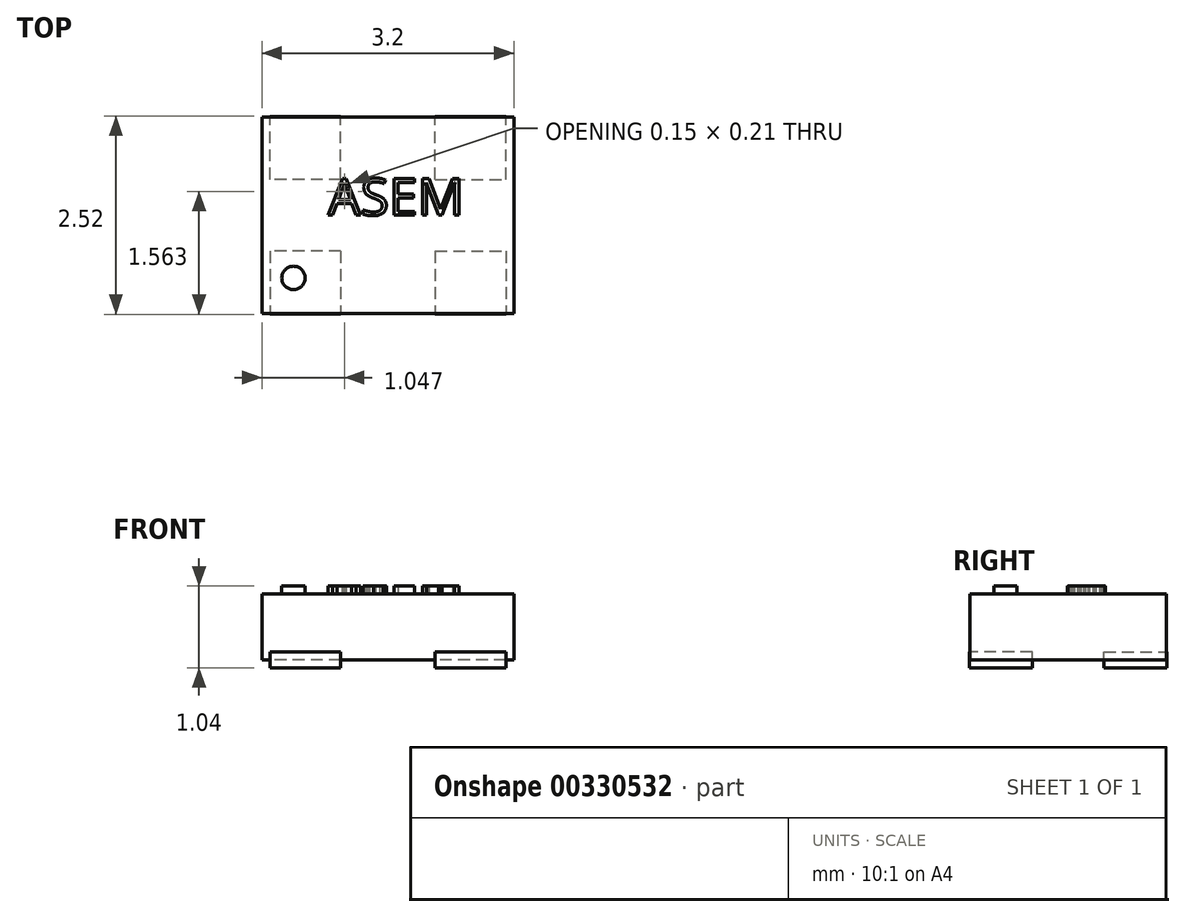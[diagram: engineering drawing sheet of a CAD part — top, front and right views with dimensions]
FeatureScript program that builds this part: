
annotation { "Feature Type Name" : "Feature", "Feature Type Description" : "" }
export const myFeature = defineFeature(function(context is Context, id is Id, definition is map)
    precondition{}
    {
        {
            var Q0;
            Q0=qCreatedBy(makeId("Top.planeOp"),FACE);
            var sketch = newSketch(context, id + "F0", { "sketchPlane" : qUnion([Q0])});
            skLineSegment(sketch, "E0.bottom", {"start": v(1.6, -1.25) * mm, "end": v(-1.6, -1.25) * mm});
            skLineSegment(sketch, "E0.top", {"start": v(1.6, 1.25) * mm, "end": v(-1.6, 1.25) * mm});
            skLineSegment(sketch, "E0.left", {"start": v(1.6, -1.25) * mm, "end": v(1.6, 1.25) * mm});
            skLineSegment(sketch, "E0.right", {"start": v(-1.6, -1.25) * mm, "end": v(-1.6, 1.25) * mm});
            skPoint(sketch, "E0.middle", {"position": v(0, 0) * mm});
            skSolve(sketch);
        }
        {
            var Q0;
            Q0 = qSketchRegion(id + "F0", true);
            extrude(context, id + "F1", {"entities" : qUnion([Q0]), "depth" : .84 * mm, "offsetDistance" : 25 * mm});
        }
        {
            var Q0;
            Q0=makeQuery(id+"F1.opExtrude","CAP_FACE",FACE,{"disambiguationData":[OSD([sQuery(id+"F0.wireOp",EDGE,"E0.bottom"),sQuery(id+"F0.wireOp",EDGE,"E0.top"),sQuery(id+"F0.wireOp",EDGE,"E0.left"),sQuery(id+"F0.wireOp",EDGE,"E0.right")])],"isStart":false});
            var sketch = newSketch(context, id + "F2", { "sketchPlane" : qUnion([Q0])});
            skCircle(sketch, "E1", {"center": v(-1.2, -0.8) * mm, "radius": 0.15 * mm});
            skText(sketch, "E2", { "text": "ASEM", "fontName": "OpenSans-Regular.ttf"});
            const initialGuessF2  = {"E2": [-0.00076, 0, 1, 0, 0.00047]};
            skSetInitialGuess(sketch, initialGuessF2);
            skSolve(sketch);
        }
        {
            var Q0;
            Q0 = qSketchRegion(id + "F2", true);
            extrude(context, id + "F3", {"entities" : qUnion([Q0]), "depth" : .1 * mm, "offsetDistance" : 25 * mm});
        }
        {
            var Q0;
            Q0=makeQuery(id+"F1.opExtrude","CAP_FACE",FACE,{"disambiguationData":[OSD([sQuery(id+"F0.wireOp",EDGE,"E0.bottom"),sQuery(id+"F0.wireOp",EDGE,"E0.top"),sQuery(id+"F0.wireOp",EDGE,"E0.left"),sQuery(id+"F0.wireOp",EDGE,"E0.right")])],"isStart":true});
            var sketch = newSketch(context, id + "F4", { "sketchPlane" : qUnion([Q0])});
            skLineSegment(sketch, "E3.bottom", {"start": v(-0.6, 0.46) * mm, "end": v(-1.5, 0.46) * mm});
            skLineSegment(sketch, "E3.top", {"start": v(-0.6, 1.26) * mm, "end": v(-1.5, 1.26) * mm});
            skLineSegment(sketch, "E3.left", {"start": v(-0.6, 0.46) * mm, "end": v(-0.6, 1.26) * mm});
            skLineSegment(sketch, "E3.right", {"start": v(-1.5, 0.46) * mm, "end": v(-1.5, 1.26) * mm});
            skPoint(sketch, "E3.middle", {"position": v(-1.05, 0.86) * mm});
            skLineSegment(sketch, "E4", {"start": v(0, 0) * mm, "end": v(0, 1.25) * mm, "construction": true});
            skPoint(sketch, "E5.MirrorP", {"position": v(1.05, 0.86) * mm});
            skLineSegment(sketch, "E6.MirrorCS", {"start": v(0.6, 0.46) * mm, "end": v(1.5, 0.46) * mm});
            skLineSegment(sketch, "E7.MirrorCS", {"start": v(0.6, 1.26) * mm, "end": v(1.5, 1.26) * mm});
            skLineSegment(sketch, "E8.MirrorCS", {"start": v(0.6, 0.46) * mm, "end": v(0.6, 1.26) * mm});
            skLineSegment(sketch, "E9.MirrorCS", {"start": v(1.5, 0.46) * mm, "end": v(1.5, 1.26) * mm});
            skLineSegment(sketch, "E10", {"start": v(-1.6, 0) * mm, "end": v(1.68, 0) * mm, "construction": true});
            skPoint(sketch, "E11.MirrorP", {"position": v(1.05, -0.86) * mm});
            skPoint(sketch, "E12.MirrorP", {"position": v(-1.05, -0.86) * mm});
            skLineSegment(sketch, "E13.MirrorCS", {"start": v(-0.6, -0.45) * mm, "end": v(-1.5, -0.46) * mm});
            skLineSegment(sketch, "E14.MirrorCS", {"start": v(-0.6, -1.25) * mm, "end": v(-1.5, -1.25) * mm});
            skLineSegment(sketch, "E15.MirrorCS", {"start": v(-0.6, -0.46) * mm, "end": v(-0.6, -1.25) * mm});
            skLineSegment(sketch, "E16.MirrorCS", {"start": v(0, 0) * mm, "end": v(0, -1.25) * mm, "construction": true});
            skLineSegment(sketch, "E17.MirrorCS", {"start": v(0.6, -0.46) * mm, "end": v(1.5, -0.46) * mm});
            skLineSegment(sketch, "E18.MirrorCS", {"start": v(0.6, -1.26) * mm, "end": v(1.5, -1.26) * mm});
            skLineSegment(sketch, "E19.MirrorCS", {"start": v(0.6, -0.46) * mm, "end": v(0.6, -1.25) * mm});
            skLineSegment(sketch, "E20.MirrorCS", {"start": v(1.5, -0.46) * mm, "end": v(1.5, -1.26) * mm});
            skLineSegment(sketch, "E21.MirrorCS", {"start": v(-1.5, -0.46) * mm, "end": v(-1.5, -1.26) * mm});
            skSolve(sketch);
        }
        {
            var Q0;
            Q0 = qSketchRegion(id + "F4", true);
            extrude(context, id + "F5", {"entities" : qUnion([Q0]), "depth" : .1 * mm, "offsetDistance" : 25 * mm, "hasSecondDirection" : true, "secondDirectionOppositeDirection" : true, "secondDirectionDepth" : .1 * mm});
        }
    });
